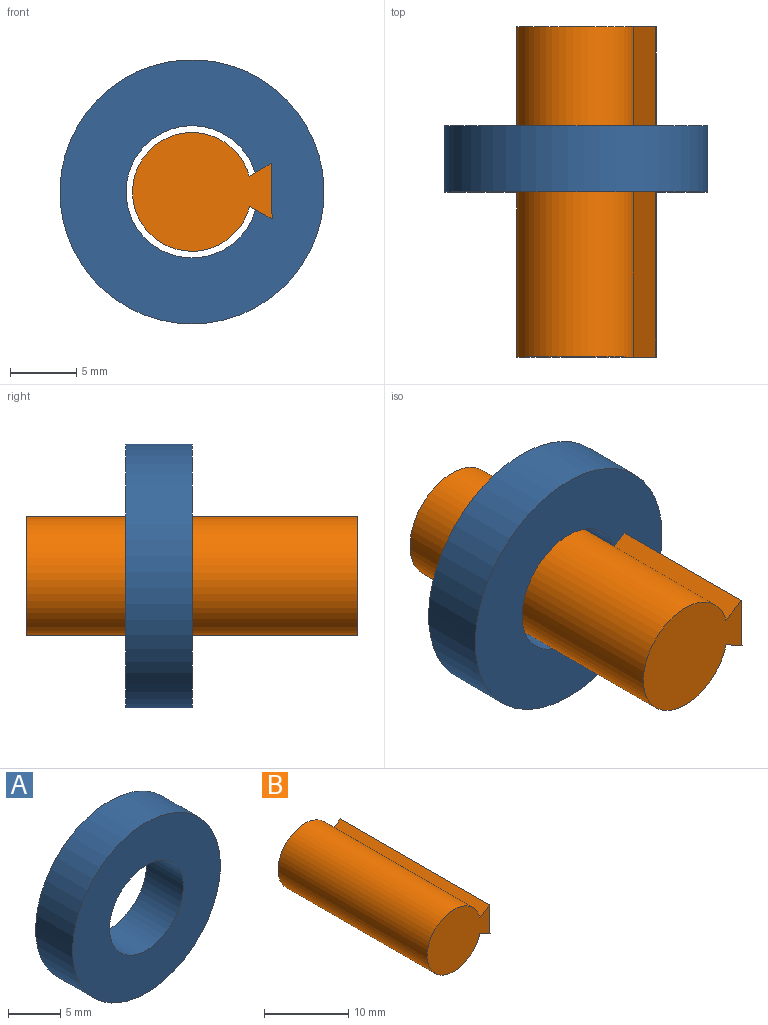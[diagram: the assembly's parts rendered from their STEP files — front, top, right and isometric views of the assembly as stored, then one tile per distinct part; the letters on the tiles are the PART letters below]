
ASSEMBLY  parts=2 mates=1
PART A: 4 faces, bbox 20x5x20 mm
  f0: cylinder r=5mm len=10mm, axis (0,1,0), area 157.1mm2, adj f2,f3
  f1: cylinder r=10mm len=20mm, axis (0,1,0), area 314.2mm2, adj f2,f3
  f2: plane 20x20mm, normal (0,-1,0), area 235.6mm2, adj f0,f1
  f3: plane 20x20mm, normal (0,1,0), area 235.6mm2, adj f0,f1
PART B: 6 faces, bbox 10.6x25x9 mm
  f0: plane 25x1.65mm, normal (-0.51,0,0.86), area 48.1mm2, adj f1,f3,f4,f5
  f1: cylinder r=4.5mm len=25mm, axis (0,1,0), area 649.3mm2, adj f0,f2,f4,f5
  f2: plane 25x1.7mm, normal (-0.49,0,-0.87), area 48.6mm2, adj f1,f3,f4,f5
  f3: plane 25x4.21mm, normal (1,0,0.02), area 105.3mm2, adj f0,f2,f4,f5
  f4: plane 10.56x9mm, normal (0,-1,0), area 68.8mm2, adj f0,f1,f2,f3
  f5: plane 10.56x9mm, normal (0,1,0), area 68.8mm2, adj f0,f1,f2,f3
PLACE A t=(-2.09,0.27,-6.34)mm
PLACE B t=(-2.09,7.77,-6.34)mm
MATE pin_slot B.f1 <-> A.f0  axis (0,1,0) through (-2.09,-4.73,-6.34)mm
